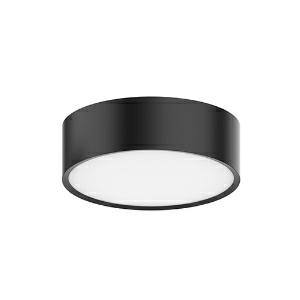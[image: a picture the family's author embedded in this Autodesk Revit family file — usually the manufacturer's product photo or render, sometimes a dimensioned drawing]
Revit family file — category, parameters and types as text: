
# Revit family: ledceilinglu-e_rd112-14w-830-bl_540001295700
name_source: partatom
category: Leuchten
revit_build: Autodesk Revit 2016 (Build: 20190508_0715(x64)
units: mm (PartAtom-declared; Revit-internal decimal feet)

## family parameters
Basisbauteil = Fläche
Beim Laden mit Abzugskörper schneiden = Nein
Bemaßung runder Anschluss = Durchmesser verwenden
Gemeinsam genutzt = Nein
Lichtquelle = Nein
Raumberechnungspunkt = Nein
Teiletyp = Normal

## types (1)
- LEDCeilingLu-E Rd112-14W-830-BL (1 x LED, 1190 lm)
    Approval mark = CE
    Beschreibung = Stylish and compact ceiling luminaire. Clean “twist-and-lock” mounting system. High quality full metal body. Low height of only 46mm. Suitable for ceiling and wall mounting.
    CIE Flux Codes = 50 80 96 100 100
    Control Gear = Electronic ballast
    Height = 100 mm  [stored 0.328084 ft]
    Hersteller = OPPLE
    Lamp Light Flux = 1190 lm
    Lamp count = 1
    Lampe = 1 x LED
    Length = 100 mm  [stored 0.328084 ft]
    Luminous efficacy = 85 lm/W
    ModVariant = Nein
    Modell = 540001295700
    Mounting Place = Wall, Ceiling
    Mounting Type = Surface mounted
    Number of Poles = 1
    OnlyDefault = Ja
    Power Factor = 1
    Product Name = LEDCeilingLu-E Rd112-14W-830-BL
    Product group = Ceiling Light Luna
    ProductGroupID = 305
    Protection Class = Protection class II
    Protection Degree = IP 20
    RLX_Detail_Level = 1
    RlxData = <blob elided: 126417 chars, md5=9aa41e25>
    Scheinlast = 14 VA
    Socket = socket
    Standby Power = 0 W
    System Light Flux = 1190 lm
    System Power = 14 W
    Typenbild = luna_bl_rd112.jpg
    Typenkommentare = Product without accessories
    URL = http://relux.com
    VarID = ---
    Voltage = 230 V
    Voltage Range = 220-240 V
    Vorgabe-Ansicht = 1800 mm
    Weight = 0.00 kg
    Width = 100 mm  [stored 0.328084 ft]

note: [stored X ft] marks values corroborated as IEEE doubles in the binary element streams (Revit-internal decimal feet)

## geometry (parser evidence)
native form markers: Blend x4, Sweep x12
no freeform markers — native parametric forms only
